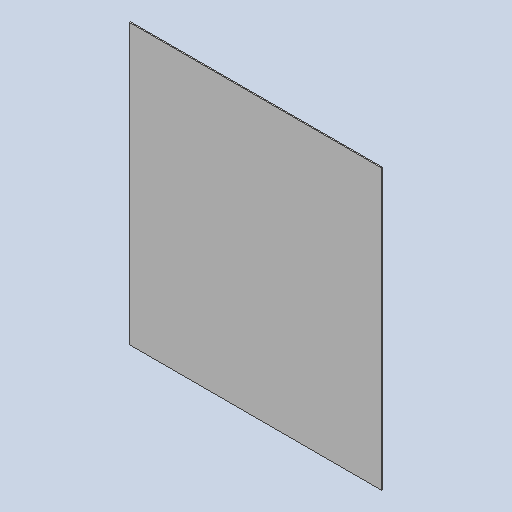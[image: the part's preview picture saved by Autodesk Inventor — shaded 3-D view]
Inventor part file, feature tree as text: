
AUTODESK INVENTOR PART (.ipt)
format: ipt  version: 2023.2 (Build 272271030, 271C)  size: 101,376 bytes
history: native  units: in
note: dims shown in document units (in); Inventor stores cm internally (conversion verified against a paired STEP export)
features: extrude x1, sketch x1
ambient origin geometry x8: Origin, YZ Plane, XZ Plane, XY Plane, X Axis, Y Axis, Z Axis, Center Point
bodies: Solid1 (feature_tree)
feature tree (2):
  extrude  "Extrusion1"  [1 undecoded]
  sketch  "Sketch1"  dims[d0=0.001in d1=0.0in]
note: 1 required parameter value undecoded (feature->parameter linkage not recoverable at this tier; creation-order binding heuristic only, values carry confidence <= 0.55)
